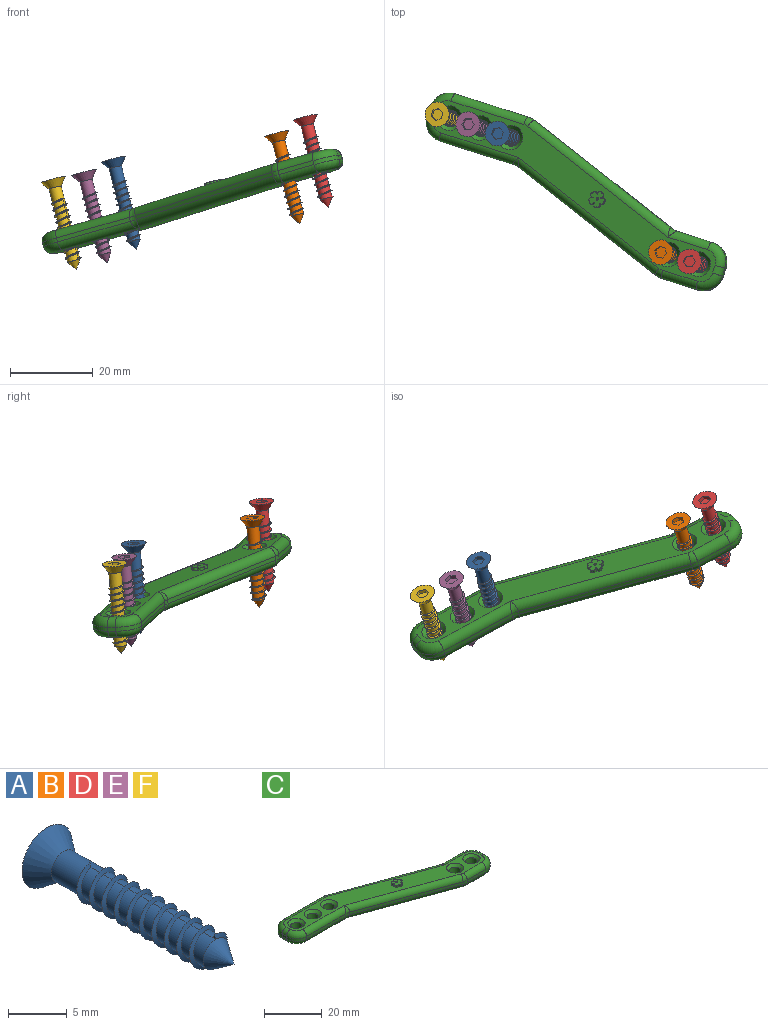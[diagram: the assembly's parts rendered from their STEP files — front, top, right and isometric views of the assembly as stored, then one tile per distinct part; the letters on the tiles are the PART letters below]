
ASSEMBLY  parts=6 mates=5
PART A: 25 faces, bbox 6x22.5x6 mm
  f0: plane 6x6mm, normal (0,1,0), area 22.4mm2, adj f1,f18,f19,f20,f21,f22,f23
  f1: cone r=3mm half-angle=36.9deg, axis (0,1,0), area 35.3mm2, adj f0,f2
  f2: cylinder r=1.5mm len=4.5mm, axis (0,1,0), area 35.3mm2, adj f1,f3,f13,f15
  f3: cylinder r=1.5mm len=3mm, axis (0,1,0), area 11.3mm2, adj f2,f4,f15,f16
  f4: cylinder r=1.5mm len=3mm, axis (0,1,0), area 11.3mm2, adj f3,f5,f15,f16
  f5: cylinder r=1.5mm len=3mm, axis (0,1,0), area 11.3mm2, adj f4,f6,f15,f16
  f6: cylinder r=1.5mm len=3mm, axis (0,1,0), area 11.3mm2, adj f5,f7,f15,f16
  f7: cylinder r=1.5mm len=3mm, axis (0,1,0), area 11.3mm2, adj f6,f8,f15,f16
  f8: cylinder r=1.5mm len=3mm, axis (0,1,0), area 11.3mm2, adj f7,f9,f15,f16
  f9: cylinder r=1.5mm len=3mm, axis (0,1,0), area 11.3mm2, adj f8,f10,f15,f16
  f10: cylinder r=1.5mm len=3mm, axis (0,1,0), area 11.3mm2, adj f9,f11,f15,f16
  f11: cylinder r=1.5mm len=3mm, axis (0,1,0), area 11.3mm2, adj f10,f12,f15,f16
  f12: cylinder r=1.5mm len=3mm, axis (0,1,0), area 7.1mm2, adj f11,f14,f16,f17
  f13: plane 0.4x0.3mm, normal (1,0,0), area 0.1mm2, adj f2,f15,f16
  f14: plane 0.4x0.3mm, normal (-1,0,0), area 0.1mm2, adj f12,f15,f16
  f15: bspline ~15.15x4.39mm, area 46mm2, adj f2,f3,f4,f5,f6,f7,f8,f9
  f16: bspline ~15.15x4.39mm, area 45.9mm2, adj f3,f4,f5,f6,f7,f8,f9,f10
  f17: cone r=1.5mm half-angle=34.3deg, axis (0,1,0), area 12.5mm2, adj f12
  f18: plane 1.5x1mm, normal (1,0,0), area 1.5mm2, adj f0,f19,f23,f24
  f19: plane 1.3x1mm, normal (0.5,0,-0.87), area 1.5mm2, adj f0,f18,f20,f24
  f20: plane 1.3x1mm, normal (-0.5,0,-0.87), area 1.5mm2, adj f0,f19,f21,f24
  f21: plane 1.5x1mm, normal (-1,0,0), area 1.5mm2, adj f0,f20,f22,f24
  f22: plane 1.3x1mm, normal (-0.5,0,0.87), area 1.5mm2, adj f0,f21,f23,f24
  f23: plane 1.3x1mm, normal (0.5,0,0.87), area 1.5mm2, adj f0,f18,f22,f24
  f24: plane 3x2.6mm, normal (0,1,0), area 5.8mm2, adj f18,f19,f20,f21,f22,f23
PART B: same geometry as A
PART C: 64 faces, bbox 83.1x28.2x5.7 mm
  f0: plane 78.29x23.39mm, normal (0,0,1), area 459.8mm2, adj f23,f24,f25,f26,f27,f28,f29,f30
  f1: plane 78.29x23.39mm, normal (0,0,-1), area 544.8mm2, adj f10,f11,f12,f13,f14,f15,f16,f17
  f2: plane 2x1mm, normal (-1,0,0), area 2mm2, adj f18,f26,f38,f44
  f3: plane 19.12x1mm, normal (0,-1,0), area 19.1mm2, adj f16,f24,f44,f51
  f4: plane 40.63x14.79mm, normal (-0.34,-0.94,0), area 43.2mm2, adj f15,f23,f47,f51
  f5: plane 9.12x1mm, normal (0,-1,0), area 9.1mm2, adj f17,f25,f41,f47
  f6: plane 2x1mm, normal (1,0,0), area 2mm2, adj f19,f27,f35,f41
  f7: plane 9.12x1mm, normal (0,1,0), area 9.1mm2, adj f21,f29,f35,f54
  f8: plane 40.63x14.79mm, normal (0.34,0.94,0), area 43.2mm2, adj f22,f30,f32,f54
  f9: plane 19.12x1mm, normal (0,1,0), area 19.1mm2, adj f20,f28,f32,f38
  f10: cylinder r=2mm len=4mm, axis (0,0,1), area 50.3mm2, adj f1,f55
  f11: cylinder r=2mm len=4mm, axis (0,0,1), area 50.3mm2, adj f1,f56
  f12: cylinder r=2mm len=4mm, axis (0,0,1), area 50.3mm2, adj f1,f57
  f13: cylinder r=2mm len=4mm, axis (0,0,1), area 50.3mm2, adj f1,f58
  f14: cylinder r=2mm len=4mm, axis (0,0,1), area 50.3mm2, adj f1,f59
  f15: cylinder r=2mm len=42.47mm, axis (0.94,-0.34,0), area 137.2mm2, adj f1,f4,f48,f50
  f16: cylinder r=2mm len=20.35mm, axis (1,0,0), area 61.5mm2, adj f1,f3,f45,f50
  f17: cylinder r=2mm len=9.12mm, axis (1,0,0), area 28.6mm2, adj f1,f5,f42,f48
  f18: cylinder r=2mm len=2mm, axis (0,-1,0), area 6.3mm2, adj f1,f2,f39,f45
  f19: cylinder r=2mm len=2mm, axis (0,1,0), area 6.3mm2, adj f1,f6,f36,f42
  f20: cylinder r=2mm len=19.12mm, axis (-1,0,0), area 60.1mm2, adj f1,f9,f33,f39
  f21: cylinder r=2mm len=10.35mm, axis (-1,0,0), area 30.1mm2, adj f1,f7,f36,f53
  f22: cylinder r=2mm len=42.47mm, axis (-0.94,0.34,0), area 137.2mm2, adj f1,f8,f33,f53
  f23: cylinder r=2mm len=42.47mm, axis (-0.94,0.34,0), area 137.2mm2, adj f0,f4,f46,f49
  f24: cylinder r=2mm len=20.35mm, axis (-1,0,0), area 61.5mm2, adj f0,f3,f43,f49
  f25: cylinder r=2mm len=9.12mm, axis (-1,0,0), area 28.6mm2, adj f0,f5,f40,f46
  f26: cylinder r=2mm len=2mm, axis (0,1,0), area 6.3mm2, adj f0,f2,f37,f43
  f27: cylinder r=2mm len=2mm, axis (0,-1,0), area 6.3mm2, adj f0,f6,f34,f40
  f28: cylinder r=2mm len=19.12mm, axis (1,0,0), area 60.1mm2, adj f0,f9,f31,f37
  f29: cylinder r=2mm len=10.35mm, axis (1,0,0), area 30.1mm2, adj f0,f7,f34,f52
  f30: cylinder r=2mm len=42.47mm, axis (0.94,-0.34,0), area 137.2mm2, adj f0,f8,f31,f52
  f31: torus R=3mm, axis (0,0,1), area 4.7mm2, adj f0,f28,f30,f32
  f32: cylinder r=5mm len=1.71mm, axis (0,0,-1), area 1.7mm2, adj f8,f9,f31,f33
  f33: torus R=3mm, axis (0,0,1), area 4.7mm2, adj f1,f20,f22,f32
  f34: torus R=3mm, axis (0,0,1), area 21.1mm2, adj f0,f27,f29,f35
  f35: cylinder r=5mm len=5mm, axis (0,0,-1), area 7.9mm2, adj f6,f7,f34,f36
  f36: torus R=3mm, axis (0,0,1), area 21.1mm2, adj f1,f19,f21,f35
  f37: torus R=3mm, axis (0,0,1), area 21.1mm2, adj f0,f26,f28,f38
  f38: cylinder r=5mm len=5mm, axis (0,0,1), area 7.9mm2, adj f2,f9,f37,f39
  f39: torus R=3mm, axis (0,0,1), area 21.1mm2, adj f1,f18,f20,f38
  f40: torus R=3mm, axis (0,0,1), area 21.1mm2, adj f0,f25,f27,f41
  f41: cylinder r=5mm len=5mm, axis (0,0,1), area 7.9mm2, adj f5,f6,f40,f42
  f42: torus R=3mm, axis (0,0,1), area 21.1mm2, adj f1,f17,f19,f41
  f43: torus R=3mm, axis (0,0,1), area 21.1mm2, adj f0,f24,f26,f44
  f44: cylinder r=5mm len=5mm, axis (0,0,-1), area 7.9mm2, adj f2,f3,f43,f45
  f45: torus R=3mm, axis (0,0,1), area 21.1mm2, adj f1,f16,f18,f44
  f46: torus R=3mm, axis (0,0,1), area 4.7mm2, adj f0,f23,f25,f47
  f47: cylinder r=5mm len=1.71mm, axis (0,0,-1), area 1.7mm2, adj f4,f5,f46,f48
  f48: torus R=3mm, axis (0,0,1), area 4.7mm2, adj f1,f15,f17,f47
  f49: bspline ~2.3x2.26mm, area 3.5mm2, adj f23,f24,f51
  f50: bspline ~2.3x2.26mm, area 3.5mm2, adj f15,f16,f51
  f51: cylinder r=5mm len=1.71mm, axis (0,0,1), area 1.7mm2, adj f3,f4,f49,f50
  f52: bspline ~2.3x2.26mm, area 3.5mm2, adj f29,f30,f54
  f53: bspline ~2.3x2.26mm, area 3.5mm2, adj f21,f22,f54
  f54: cylinder r=5mm len=1.71mm, axis (0,0,1), area 1.7mm2, adj f7,f8,f52,f53
  f55: cone r=2mm half-angle=45deg, axis (0,0,1), area 22.2mm2, adj f0,f10
  f56: cone r=2mm half-angle=45deg, axis (0,0,1), area 22.2mm2, adj f0,f11
  f57: cone r=2mm half-angle=45deg, axis (0,0,1), area 22.2mm2, adj f0,f12
  f58: cone r=2mm half-angle=45deg, axis (0,0,1), area 22.2mm2, adj f0,f13
  f59: cone r=2mm half-angle=45deg, axis (0,0,1), area 22.2mm2, adj f0,f14
  f60: extruded ~0.7x0.63mm, area 1.4mm2, adj f62,f63
  f61: extruded ~3.96x3.83mm, area 11.7mm2, adj f0,f62
  f62: plane 4.09x3.97mm, normal (0,0,1), area 9.9mm2, adj f60,f61
  f63: plane 0.65x0.64mm, normal (0,0,1), area 0.3mm2, adj f60
PART D: same geometry as A
PART E: same geometry as A
PART F: same geometry as A
PLACE A rot(axis=(0.32,-0.72,-0.61),160.3deg) t=(-97.9,65.54,-15.51)mm
PLACE B rot(axis=(0.18,-0.73,-0.66),178.5deg) t=(-58.48,36.88,-9.3)mm
PLACE C rot(axis=(-0.09,-0.65,-0.76),23.1deg) t=(-111.87,76.38,-38.57)mm
PLACE D rot(axis=(0.49,0.56,0.66),110.5deg) t=(-51.59,34.68,-5.36)mm
PLACE E rot(axis=(0.1,0.71,0.7),147.4deg) t=(-104.96,67.8,-18.74)mm
PLACE F rot(axis=(0.82,0.29,0.49),90.6deg) t=(-112.43,70.17,-20.4)mm
MATE cylindrical E.f1 <-> C.f13  axis (-0.25,0.07,0.97) through (-104.47,67.65,-20.67)mm
MATE cylindrical F.f1 <-> C.f14  axis (-0.25,0.07,0.97) through (-111.94,70.03,-22.33)mm
MATE cylindrical B.f1 <-> C.f11  axis (-0.25,0.07,0.97) through (-57.98,36.73,-11.23)mm
MATE cylindrical A.f1 <-> C.f12  axis (-0.25,0.07,0.97) through (-97.4,65.4,-17.44)mm
MATE cylindrical D.f1 <-> C.f10  axis (-0.25,0.07,0.97) through (-51.1,34.53,-7.29)mm
